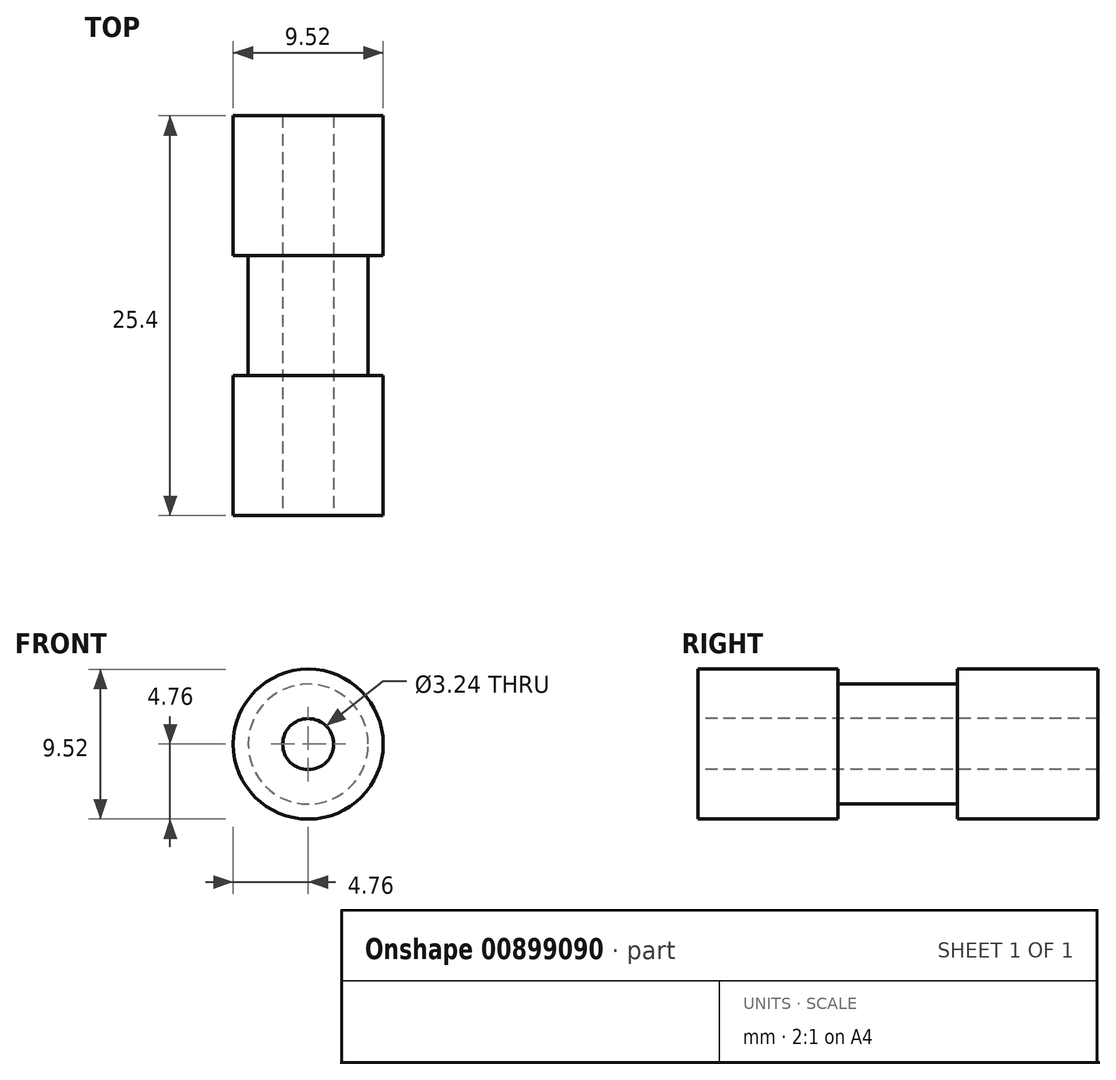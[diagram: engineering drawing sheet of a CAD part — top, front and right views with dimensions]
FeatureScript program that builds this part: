
annotation { "Feature Type Name" : "Feature", "Feature Type Description" : "" }
export const myFeature = defineFeature(function(context is Context, id is Id, definition is map)
    precondition{}
    {
        {
            var Q0;
            Q0=qCreatedBy(makeId("Right.planeOp"),FACE);
            var sketch = newSketch(context, id + "F0", { "sketchPlane" : qUnion([Q0])});
            skLineSegment(sketch, "E0", {"start": v(-12.7, 1.62) * mm, "end": v(-12.7, 4.76) * mm});
            skLineSegment(sketch, "E1", {"start": v(-12.7, 4.76) * mm, "end": v(-3.81, 4.76) * mm});
            skLineSegment(sketch, "E2", {"start": v(-3.81, 4.76) * mm, "end": v(-3.81, 4.76) * mm});
            skLineSegment(sketch, "E3", {"start": v(-3.81, 4.76) * mm, "end": v(-3.81, 3.81) * mm});
            skLineSegment(sketch, "E4", {"start": v(-3.81, 3.81) * mm, "end": v(3.81, 3.81) * mm});
            skLineSegment(sketch, "E5", {"start": v(3.81, 3.81) * mm, "end": v(3.81, 3.81) * mm});
            skLineSegment(sketch, "E6", {"start": v(3.81, 4.76) * mm, "end": v(3.81, 3.81) * mm});
            skLineSegment(sketch, "E7", {"start": v(3.8, 4.76) * mm, "end": v(12.7, 4.76) * mm});
            skLineSegment(sketch, "E8", {"start": v(12.7, 4.76) * mm, "end": v(12.7, 4.76) * mm});
            skLineSegment(sketch, "E9", {"start": v(12.7, 4.76) * mm, "end": v(12.7, 1.62) * mm});
            skLineSegment(sketch, "E10", {"start": v(12.7, 0) * mm, "end": v(12.7, 0) * mm});
            skLineSegment(sketch, "E11", {"start": v(12.7, 1.62) * mm, "end": v(-12.7, 1.62) * mm});
            skLineSegment(sketch, "E12", {"start": v(-12.7, 0) * mm, "end": v(12.7, 0) * mm, "construction": true});
            skSolve(sketch);
        }
        {
            var Q0;
            Q0=makeQuery(id+"F0.imprint","IMPRINT",FACE,{"disambiguationData":[TD([[makeQuery(id+"F0.imprint","IMPRINT",EDGE,{"derivedFrom":sQuery(id+"F0.wireOp",EDGE,"E0")}),-1.0]])]});
            var Q1;
            Q1=sQuery(id+"F0.wireOp",EDGE,"E12");
            revolve(context, id + "F1", {"surfaceOperationType" : NewSurfaceOperationType.NEW, "entities" : qUnion([Q0]), "axis" : qUnion([Q1]), "revolveType" : RevolveType.FULL});
        }
    });
